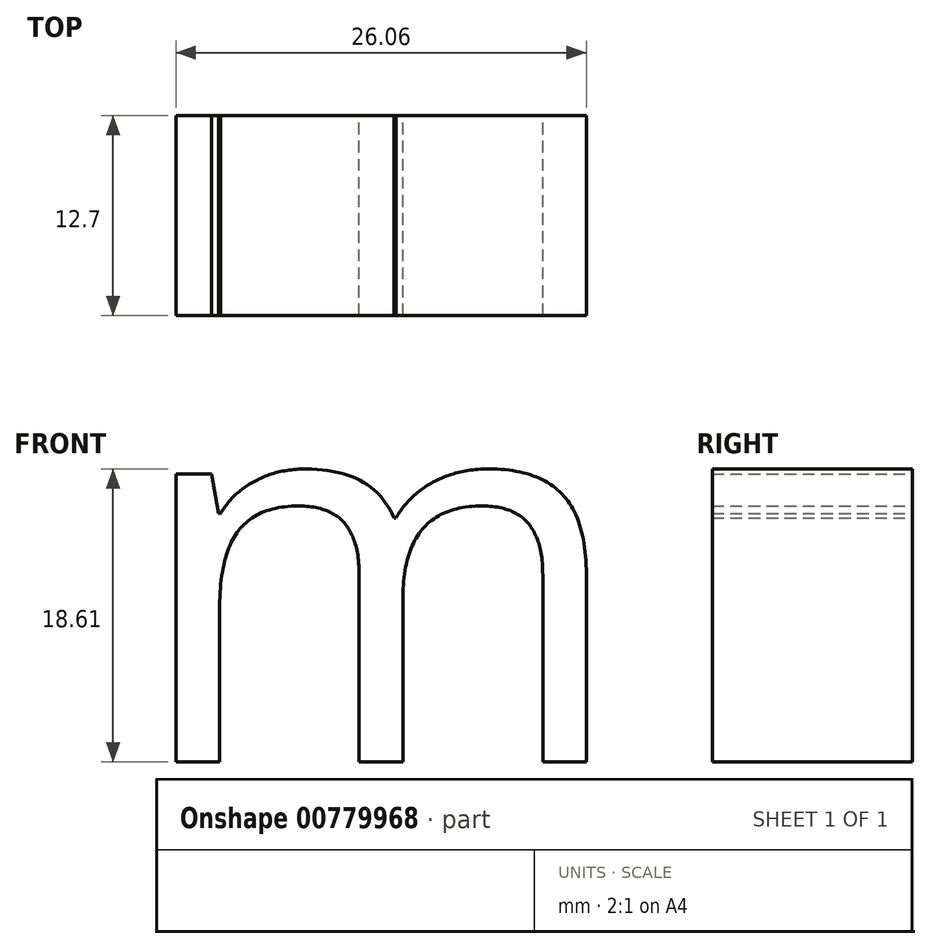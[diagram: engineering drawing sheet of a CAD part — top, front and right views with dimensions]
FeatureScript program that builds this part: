
annotation { "Feature Type Name" : "Feature", "Feature Type Description" : "" }
export const myFeature = defineFeature(function(context is Context, id is Id, definition is map)
    precondition{}
    {
        {
            var Q0;
            Q0=qCreatedBy(makeId("Front.planeOp"),FACE);
            var sketch = newSketch(context, id + "F0", { "sketchPlane" : qUnion([Q0])});
            skText(sketch, "E0", { "text": "m", "fontName": "OpenSans-Regular.ttf"});
            const initialGuessF0  = {"E0": [-0.05897, 0, 1, 0, 0.02459]};
            skSetInitialGuess(sketch, initialGuessF0);
            skSolve(sketch);
        }
        {
            var Q0;
            Q0 = qSketchRegion(id + "F0", true);
            extrude(context, id + "F1", {"entities" : qUnion([Q0]), "depth" : 12.7 * mm, "offsetDistance" : 25.4 * mm});
        }
    });
